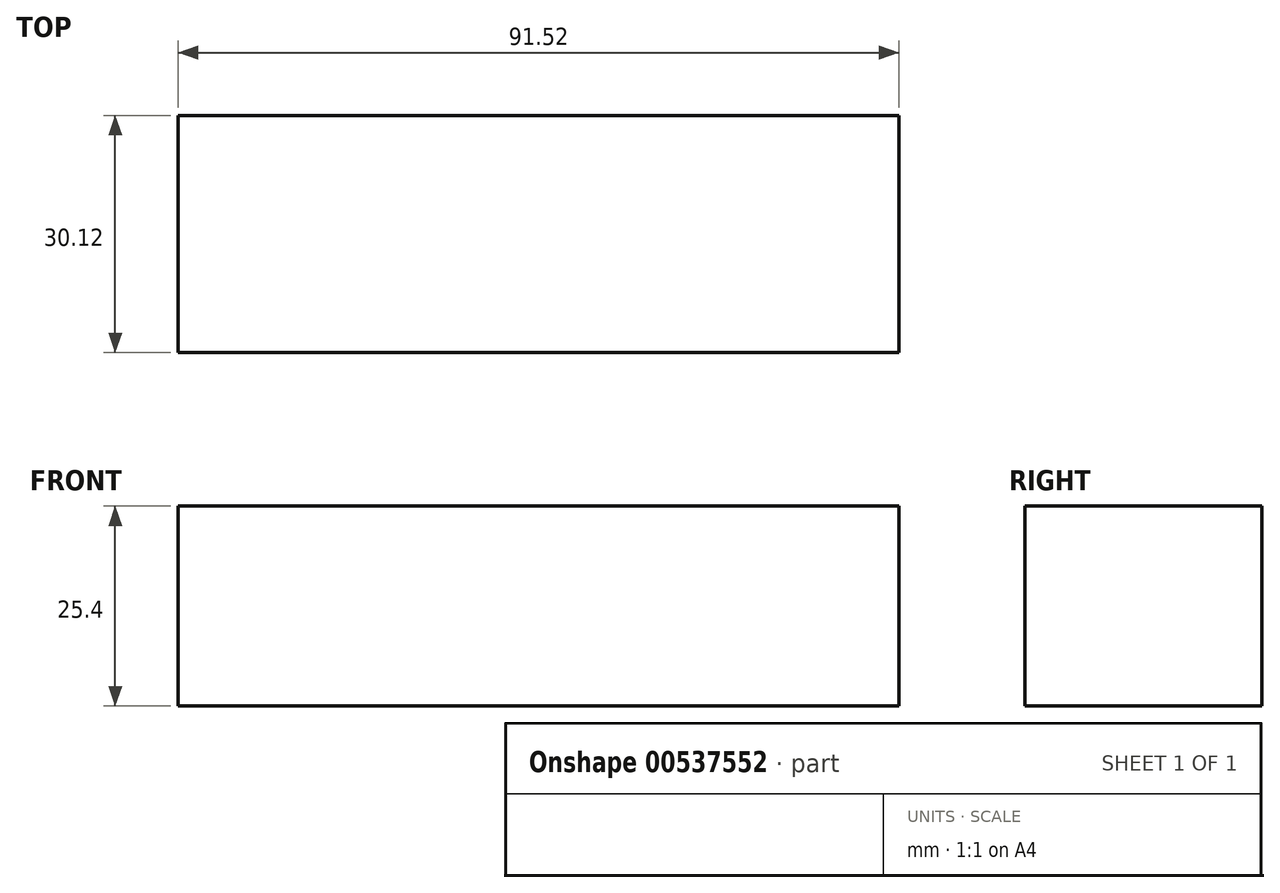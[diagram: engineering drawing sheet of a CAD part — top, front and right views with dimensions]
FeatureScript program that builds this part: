
annotation { "Feature Type Name" : "Feature", "Feature Type Description" : "" }
export const myFeature = defineFeature(function(context is Context, id is Id, definition is map)
    precondition{}
    {
        {
            var Q0;
            Q0=qCreatedBy(makeId("Top.planeOp"),FACE);
            var sketch = newSketch(context, id + "F0", { "sketchPlane" : qUnion([Q0])});
            skLineSegment(sketch, "E0.bottom", {"start": v(45.76, 15.06) * mm, "end": v(-45.76, 15.06) * mm});
            skLineSegment(sketch, "E0.top", {"start": v(45.76, -15.06) * mm, "end": v(-45.76, -15.06) * mm});
            skLineSegment(sketch, "E0.left", {"start": v(45.76, 15.06) * mm, "end": v(45.76, -15.06) * mm});
            skLineSegment(sketch, "E0.right", {"start": v(-45.76, 15.06) * mm, "end": v(-45.76, -15.06) * mm});
            skPoint(sketch, "E0.middle", {"position": v(0, 0) * mm});
            skSolve(sketch);
        }
        {
            var Q0;
            Q0=makeQuery(id+"F0.imprint","IMPRINT",FACE,{"disambiguationData":[TD([[makeQuery(id+"F0.imprint","IMPRINT",EDGE,{"derivedFrom":sQuery(id+"F0.wireOp",EDGE,"E0.bottom")}),1.0]])]});
            extrude(context, id + "F1", {"entities" : qUnion([Q0]), "depth" : 25.4 * mm, "offsetDistance" : 25.4 * mm});
        }
    });
